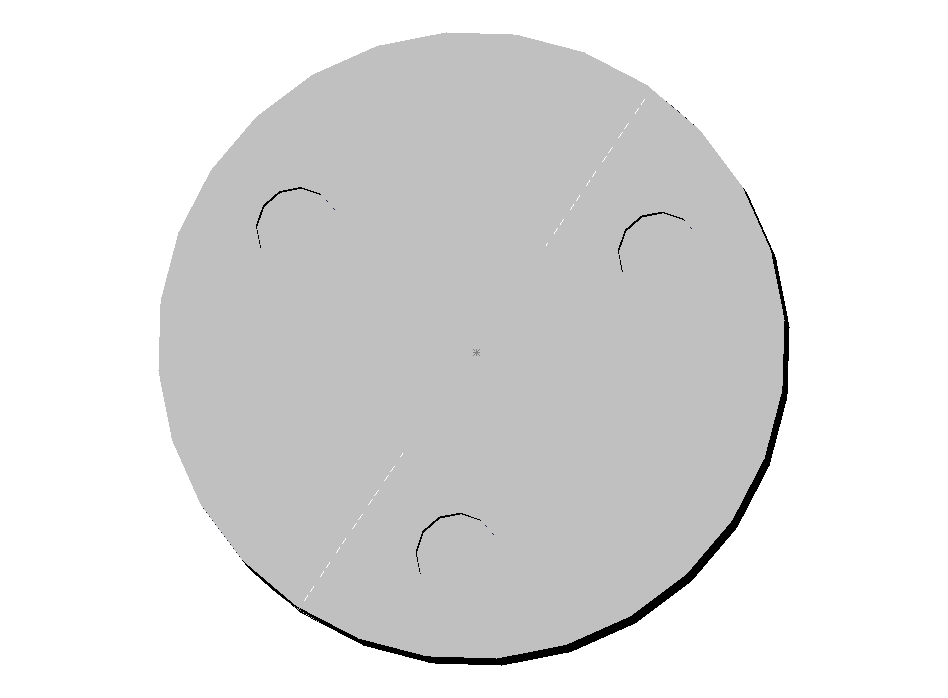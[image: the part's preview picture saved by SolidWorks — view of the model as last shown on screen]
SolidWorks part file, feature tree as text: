
SOLIDWORKS PART (.sldprt)
format: sldprt  version: not decoded by parser v0  size: 145,920 bytes
history: native  units: mm
features: sketch x5, cut_extrude x4, plane x3, extrude x1, pattern_circular x1 (+5 scaffold rows collapsed)
feature tree (19):
  scaffold x5  (default folders/planes/origin — collapsed)
  plane  "Plane1"
  plane  "Plane2"
  plane  "Plane3"
  sketch  "Sketch1"  dims[D1=30.0mm D2=30.0mm]
  extrude  "Base-Extrude"  Depth=30mm
  sketch  "Sketch2"  dims[D1=12.0mm D2=30.0mm]
  cut_extrude  "Cut-Extrude1"  Depth=25mm
  sketch  "Sketch4"  dims[D1=3.25mm D2=17.5mm D3=15.0mm]
  cut_extrude  "Cut-Extrude3"  [1 undecoded]
  sketch  "Sketch5"  dims[D1=3.25mm D2=7.5mm D3=15.0mm]
  cut_extrude  "Cut-Extrude4"  [1 undecoded]
  sketch  "Sketch6"  dims[D1=4.0mm D3=~5.027544mm D2=10.0mm]
  cut_extrude  "Cut-Extrude5"  Depth=7mm
  pattern_circular  "CirPattern1"  Count=3 Angle=360deg
decode coverage: 9 of 11 modeling features carry decoded parameters
note: ~ marks probable driven/reference dimensions
note: 2 parameter values undecoded
note: suppression state not decoded; provenance and decode notes live in map.json
